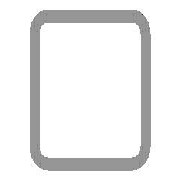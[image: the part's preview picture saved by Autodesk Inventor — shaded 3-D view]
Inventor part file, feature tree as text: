
AUTODESK INVENTOR PART (.ipt)
format: ipt  version: 2019 (Build 230136000, 136)  size: 133,632 bytes
history: native  units: mm (DEFAULTED — no unit token found)
features: other x4, sketch x3, plane x2, split x1
ambient origin geometry x8: Origin, YZ Plane, XZ Plane, XY Plane, X Axis, Y Axis, Z Axis, Center Point
bodies: Solid1 (feature_tree), Body (feature_tree)
feature tree (10):
  parser-record x1  (decoder bookkeeping rows leaked as tree rows — omitted from the tree; the rows remain in map.json)
  other  "Driven Length"
  other  "Start plane"
  other  "End plane"
  plane  "Work Plane4"
  split  "Split1"
  sketch  "Sketch"  dims[d7=4.0mm d9=20.0mm d11=20.0mm d12=2.0mm d13=-0.0mm d14=1080.0mm d15=10.0mm d16=10.0mm d17=90.0deg d18=1080.0mm]
  sketch  "Sketch3"  dims[d3=1080.0mm]
  plane  "Work Plane3"
  sketch  "Sketch4"  dims[d4=0.0mm]
